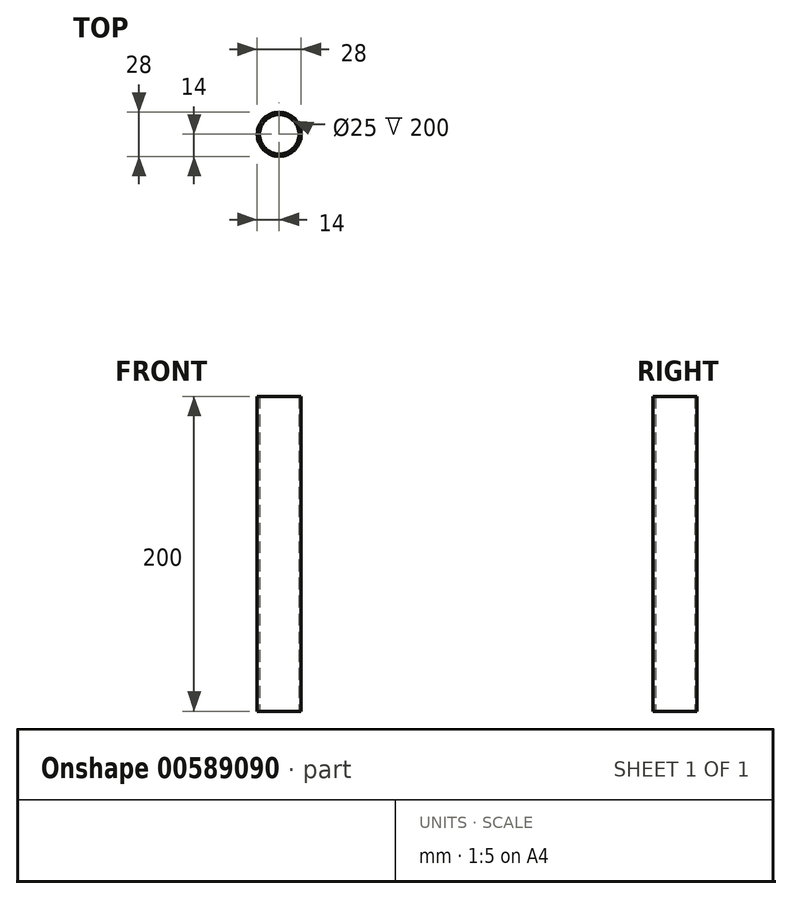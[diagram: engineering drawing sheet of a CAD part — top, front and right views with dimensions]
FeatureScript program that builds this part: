
annotation { "Feature Type Name" : "Feature", "Feature Type Description" : "" }
export const myFeature = defineFeature(function(context is Context, id is Id, definition is map)
    precondition{}
    {
        {
            var Q0;
            Q0=qCreatedBy(makeId("Top.planeOp"),FACE);
            var sketch = newSketch(context, id + "F0", { "sketchPlane" : qUnion([Q0])});
            skCircle(sketch, "E0", {"center": v(0, 0) * mm, "radius": 14 * mm});
            skCircle(sketch, "E1", {"center": v(0, 0) * mm, "radius": 12.5 * mm});
            skSolve(sketch);
        }
        {
            var Q0;
            Q0=qSketchRegion(id+"F0",true);
            extrude(context, id + "F1", {"entities" : qUnion([Q0]), "depth" : 200 * mm, "offsetDistance" : 25 * mm});
        }
    });
